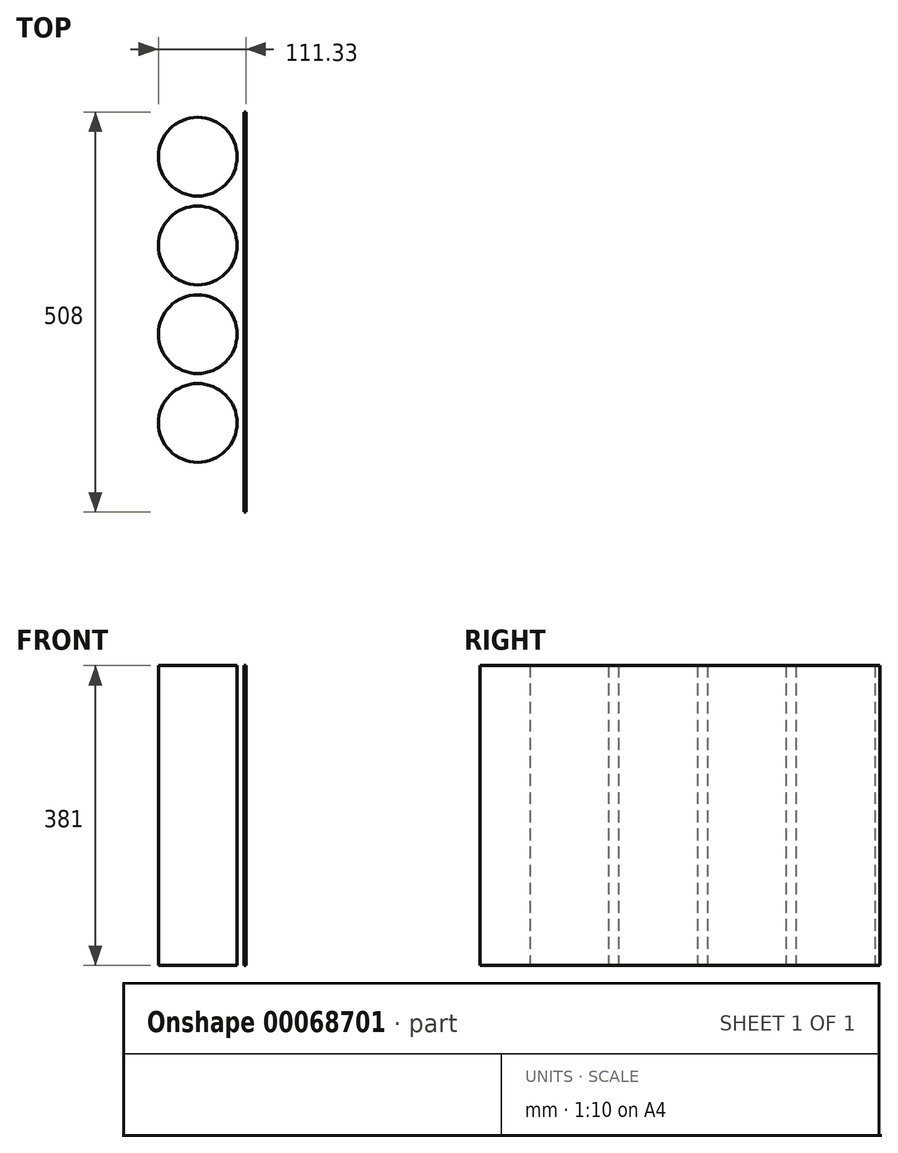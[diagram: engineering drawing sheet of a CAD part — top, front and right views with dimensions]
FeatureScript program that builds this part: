
annotation { "Feature Type Name" : "Feature", "Feature Type Description" : "" }
export const myFeature = defineFeature(function(context is Context, id is Id, definition is map)
    precondition{}
    {
        {
            var Q0;
            Q0=qCreatedBy(makeId("Right.planeOp"),FACE);
            var sketch = newSketch(context, id + "F0", { "sketchPlane" : qUnion([Q0])});
            skLineSegment(sketch, "E0.rect.bottom", {"start": v(-254, 190.5) * mm, "end": v(254, 190.5) * mm});
            skLineSegment(sketch, "E0.rect.top", {"start": v(-254, -190.5) * mm, "end": v(254, -190.5) * mm});
            skLineSegment(sketch, "E0.rect.left", {"start": v(-254, 190.5) * mm, "end": v(-254, -190.5) * mm});
            skLineSegment(sketch, "E0.rect.right", {"start": v(254, 190.5) * mm, "end": v(254, -190.5) * mm});
            skPoint(sketch, "E0.rect.middle", {"position": v(0, 0) * mm});
            skSolve(sketch);
        }
        {
            var Q0;
            Q0 = qSketchRegion(id + "F0", true);
            extrude(context, id + "F1", {"entities" : qUnion([Q0]), "depth" : 2.54 * mm});
        }
        {
            var Q0;
            Q0=qCreatedBy(makeId("Top.planeOp"),FACE);
            var sketch = newSketch(context, id + "F2", { "sketchPlane" : qUnion([Q0])});
            skLineSegment(sketch, "E1", {"start": v(-58.78, 197.38) * mm, "end": v(-58.78, -197.38) * mm, "construction": true});
            skCircle(sketch, "E2", {"center": v(-58.78, 197.38) * mm, "radius": 50.01 * mm});
            skCircle(sketch, "E3", {"center": v(-58.78, 84.66) * mm, "radius": 50.01 * mm});
            skCircle(sketch, "E4", {"center": v(-58.78, -28.07) * mm, "radius": 50.01 * mm});
            skCircle(sketch, "E5", {"center": v(-58.78, -140.8) * mm, "radius": 50.01 * mm});
            skSolve(sketch);
        }
        {
            var Q0;
            Q0 = qSketchRegion(id + "F2", true);
            extrude(context, id + "F3", {"entities" : qUnion([Q0]), "endBound" : BoundingType.SYMMETRIC, "depth" : 381 * mm});
        }
    });
